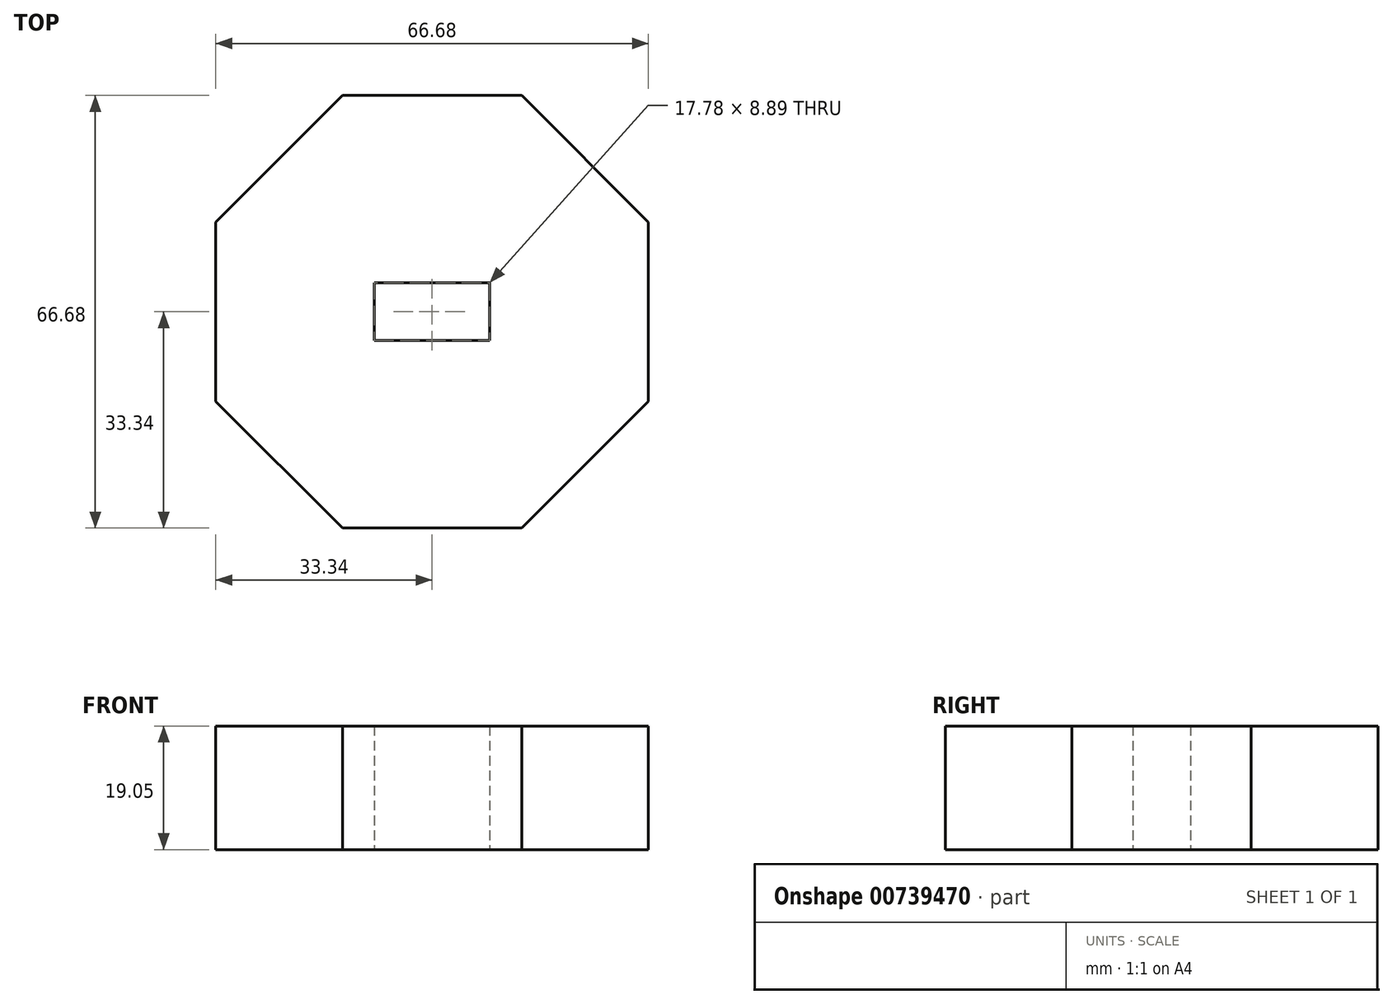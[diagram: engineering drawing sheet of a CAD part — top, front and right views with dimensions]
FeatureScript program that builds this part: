
annotation { "Feature Type Name" : "Feature", "Feature Type Description" : "" }
export const myFeature = defineFeature(function(context is Context, id is Id, definition is map)
    precondition{}
    {
        {
            var Q0;
            Q0=qCreatedBy(makeId("Top.planeOp"),FACE);
            var sketch = newSketch(context, id + "F0", { "sketchPlane" : qUnion([Q0])});
            skCircle(sketch, "E0.cCircle", {"center": v(0, 0) * mm, "radius": 33.34 * mm, "construction": true});
            skLineSegment(sketch, "E0.0", {"start": v(33.34, -13.8) * mm, "end": v(13.8, -33.34) * mm});
            skLineSegment(sketch, "E0.1", {"start": v(13.8, -33.34) * mm, "end": v(-13.8, -33.34) * mm});
            skLineSegment(sketch, "E0.2", {"start": v(-13.8, -33.34) * mm, "end": v(-33.34, -13.8) * mm});
            skLineSegment(sketch, "E0.3", {"start": v(-33.34, -13.8) * mm, "end": v(-33.34, 13.8) * mm});
            skLineSegment(sketch, "E0.4", {"start": v(-33.34, 13.8) * mm, "end": v(-13.8, 33.34) * mm});
            skLineSegment(sketch, "E0.5", {"start": v(-13.8, 33.34) * mm, "end": v(13.8, 33.34) * mm});
            skLineSegment(sketch, "E0.6", {"start": v(13.8, 33.34) * mm, "end": v(33.34, 13.8) * mm});
            skLineSegment(sketch, "E0.7", {"start": v(33.34, 13.8) * mm, "end": v(33.34, -13.8) * mm});
            skPoint(sketch, "E0.0.midPoint", {"position": v(23.57, -23.57) * mm});
            skLineSegment(sketch, "E1.top", {"start": v(4.45, 8.9) * mm, "end": v(-4.44, 8.9) * mm});
            skLineSegment(sketch, "E1.left", {"start": v(4.44, -8.9) * mm, "end": v(4.45, 8.9) * mm});
            skLineSegment(sketch, "E1.right", {"start": v(-4.45, -8.9) * mm, "end": v(-4.44, 8.9) * mm});
            skLineSegment(sketch, "E2", {"start": v(23.57, 23.57) * mm, "end": v(4.44, 8.9) * mm});
            skLineSegment(sketch, "E3", {"start": v(23.57, -23.57) * mm, "end": v(4.44, -8.9) * mm});
            skLineSegment(sketch, "E4", {"start": v(-23.57, -23.57) * mm, "end": v(-4.44, -8.9) * mm});
            skLineSegment(sketch, "E5", {"start": v(-23.57, 23.57) * mm, "end": v(-4.44, 8.9) * mm});
            skLineSegment(sketch, "E6.bottom", {"start": v(-4.45, -4.45) * mm, "end": v(4.45, -4.45) * mm});
            skLineSegment(sketch, "E6.top", {"start": v(-4.45, 4.45) * mm, "end": v(4.45, 4.45) * mm});
            skLineSegment(sketch, "E6.left", {"start": v(-4.45, -4.45) * mm, "end": v(-4.45, 4.45) * mm});
            skLineSegment(sketch, "E6.right", {"start": v(4.45, -4.45) * mm, "end": v(4.45, 4.45) * mm});
            skLineSegment(sketch, "E7", {"start": v(-4.45, -8.9) * mm, "end": v(4.44, -8.9) * mm});
            skLineSegment(sketch, "E8.bottom", {"start": v(-8.89, -4.45) * mm, "end": v(8.9, -4.45) * mm});
            skLineSegment(sketch, "E8.top", {"start": v(-8.9, 4.45) * mm, "end": v(8.89, 4.45) * mm});
            skLineSegment(sketch, "E8.left", {"start": v(-8.9, -4.45) * mm, "end": v(-8.9, 4.45) * mm});
            skLineSegment(sketch, "E8.right", {"start": v(8.9, -4.45) * mm, "end": v(8.9, 4.45) * mm});
            skLineSegment(sketch, "E9", {"start": v(23.57, -23.57) * mm, "end": v(8.89, -4.44) * mm});
            skLineSegment(sketch, "E10", {"start": v(23.57, 23.57) * mm, "end": v(8.89, 4.45) * mm});
            skLineSegment(sketch, "E11", {"start": v(-23.57, -23.57) * mm, "end": v(-8.9, -4.45) * mm});
            skLineSegment(sketch, "E12", {"start": v(-23.57, 23.57) * mm, "end": v(-8.9, 4.45) * mm});
            skSolve(sketch);
        }
        {
            var Q0;
            {var subQ0=sQuery(id+"F0.wireOp",EDGE,"E6.right");Q0=makeQuery(id+"F0.imprint","IMPRINT",FACE,{"disambiguationData":[TD([[makeQuery(id+"F0.imprint","IMPRINT",EDGE,{"derivedFrom":subQ0}),-1.0]])]});}
            var Q1;
            {var subQ0=sQuery(id+"F0.wireOp",EDGE,"E0.7");Q1=makeQuery(id+"F0.imprint","IMPRINT",FACE,{"disambiguationData":[TD([[makeQuery(id+"F0.imprint","IMPRINT",EDGE,{"derivedFrom":subQ0}),-1.0]])]});}
            var Q2;
            {var subQ0=sQuery(id+"F0.wireOp",EDGE,"E3");Q2=makeQuery(id+"F0.imprint","IMPRINT",FACE,{"disambiguationData":[TD([[makeQuery(id+"F0.imprint","IMPRINT",EDGE,{"derivedFrom":subQ0}),-1.0]])]});}
            var Q3;
            {var subQ0=sQuery(id+"F0.wireOp",EDGE,"E2");Q3=makeQuery(id+"F0.imprint","IMPRINT",FACE,{"disambiguationData":[TD([[makeQuery(id+"F0.imprint","IMPRINT",EDGE,{"derivedFrom":subQ0}),1.0]])]});}
            var Q4;
            {var subQ0=sQuery(id+"F0.wireOp",EDGE,"E7");Q4=makeQuery(id+"F0.imprint","IMPRINT",FACE,{"disambiguationData":[TD([[makeQuery(id+"F0.imprint","IMPRINT",EDGE,{"derivedFrom":subQ0}),1.0]])]});}
            var Q5;
            {var subQ1=sQuery(id+"F0.wireOp",EDGE,"E0.3");Q5=makeQuery(id+"F0.imprint","IMPRINT",FACE,{"disambiguationData":[TD([[makeQuery(id+"F0.imprint","IMPRINT",EDGE,{"derivedFrom":subQ1}),-1.0]])]});}
            var Q6;
            {var subQ0=sQuery(id+"F0.wireOp",EDGE,"E4");Q6=makeQuery(id+"F0.imprint","IMPRINT",FACE,{"disambiguationData":[TD([[makeQuery(id+"F0.imprint","IMPRINT",EDGE,{"derivedFrom":subQ0}),1.0]])]});}
            var Q7;
            {var subQ0=sQuery(id+"F0.wireOp",EDGE,"E6.left");Q7=makeQuery(id+"F0.imprint","IMPRINT",FACE,{"disambiguationData":[TD([[makeQuery(id+"F0.imprint","IMPRINT",EDGE,{"derivedFrom":subQ0}),1.0]])]});}
            var Q8;
            {var subQ0=sQuery(id+"F0.wireOp",EDGE,"E1.top");Q8=makeQuery(id+"F0.imprint","IMPRINT",FACE,{"disambiguationData":[TD([[makeQuery(id+"F0.imprint","IMPRINT",EDGE,{"derivedFrom":subQ0}),1.0]])]});}
            var Q9;
            {var subQ2=sQuery(id+"F0.wireOp",EDGE,"E0.1");Q9=makeQuery(id+"F0.imprint","IMPRINT",FACE,{"disambiguationData":[TD([[makeQuery(id+"F0.imprint","IMPRINT",EDGE,{"derivedFrom":subQ2}),-1.0]])]});}
            var Q10;
            {var subQ0=sQuery(id+"F0.wireOp",EDGE,"E5");Q10=makeQuery(id+"F0.imprint","IMPRINT",FACE,{"disambiguationData":[TD([[makeQuery(id+"F0.imprint","IMPRINT",EDGE,{"derivedFrom":subQ0}),-1.0]])]});}
            var Q11;
            {var subQ1=sQuery(id+"F0.wireOp",EDGE,"E0.5");Q11=makeQuery(id+"F0.imprint","IMPRINT",FACE,{"disambiguationData":[TD([[makeQuery(id+"F0.imprint","IMPRINT",EDGE,{"derivedFrom":subQ1}),-1.0]])]});}
            var Q12;
            {var subQ0=sQuery(id+"F0.wireOp",EDGE,"E6.left");Q12=makeQuery(id+"F0.imprint","IMPRINT",FACE,{"disambiguationData":[TD([[makeQuery(id+"F0.imprint","IMPRINT",EDGE,{"derivedFrom":subQ0}),-1.0]])]});}
            extrude(context, id + "F1", {"entities" : qUnion([Q0, Q1, Q2, Q3, Q4, Q5, Q6, Q7, Q8, Q9, Q10, Q11, Q12]), "depth" : 19.05 * mm, "offsetDistance" : 25.4 * mm});
        }
    });
